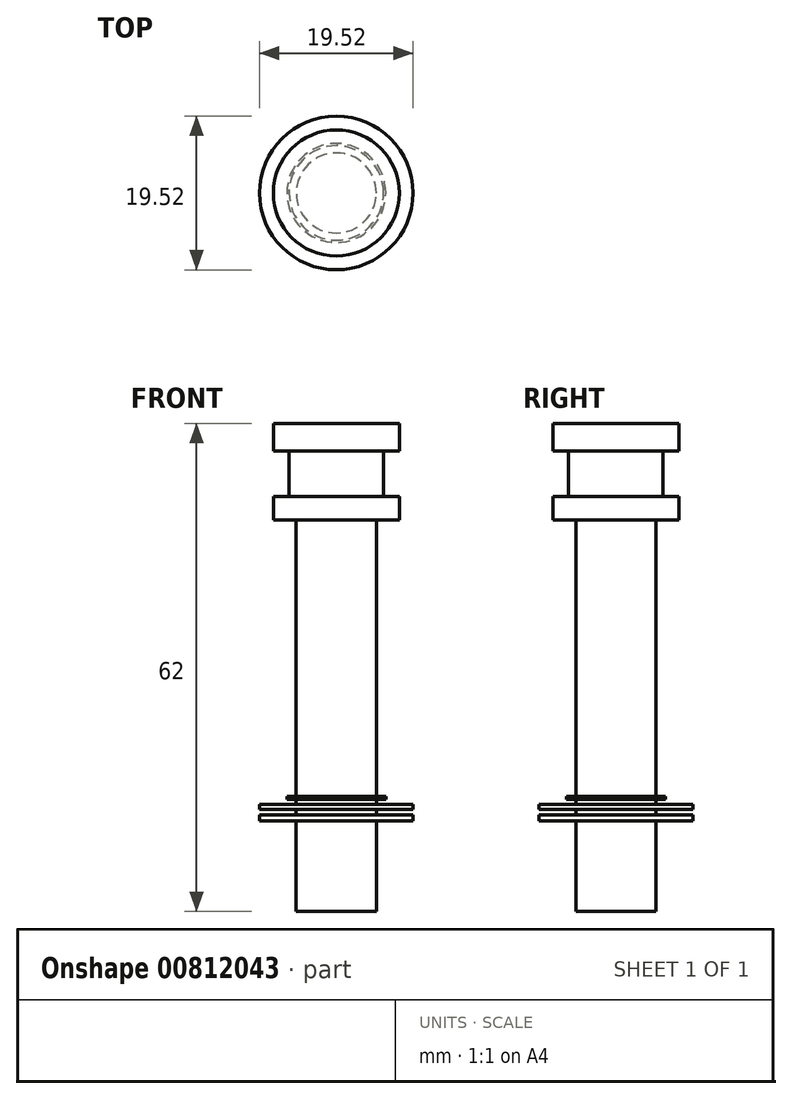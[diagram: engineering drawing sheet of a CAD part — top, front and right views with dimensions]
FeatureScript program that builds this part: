
annotation { "Feature Type Name" : "Feature", "Feature Type Description" : "" }
export const myFeature = defineFeature(function(context is Context, id is Id, definition is map)
    precondition{}
    {
        {
            var Q0;
            Q0=qCreatedBy(makeId("Front.planeOp"),FACE);
            var sketch = newSketch(context, id + "F0", { "sketchPlane" : qUnion([Q0])});
            skLineSegment(sketch, "E0", {"start": v(0, 0) * mm, "end": v(-8, 0) * mm});
            skLineSegment(sketch, "E1", {"start": v(-8, 0) * mm, "end": v(-8, -3.5) * mm});
            skLineSegment(sketch, "E2", {"start": v(-8, -3.5) * mm, "end": v(-6, -3.5) * mm});
            skLineSegment(sketch, "E3", {"start": v(-6, -3.5) * mm, "end": v(-6, -9.3) * mm});
            skLineSegment(sketch, "E4", {"start": v(-6, -9.3) * mm, "end": v(-8, -9.3) * mm});
            skLineSegment(sketch, "E5", {"start": v(-8, -9.3) * mm, "end": v(-8, -12.3) * mm});
            skLineSegment(sketch, "E6", {"start": v(-8, -12.3) * mm, "end": v(-5.09, -12.3) * mm});
            skLineSegment(sketch, "E7", {"start": v(-5.09, -12.3) * mm, "end": v(-5.09, -47.38) * mm});
            skLineSegment(sketch, "E8", {"start": v(-5.09, -47.38) * mm, "end": v(-6.29, -47.38) * mm});
            skLineSegment(sketch, "E9", {"start": v(-6.29, -47.38) * mm, "end": v(-6.29, -47.8) * mm});
            skLineSegment(sketch, "E10", {"start": v(-6.29, -47.8) * mm, "end": v(-5.09, -47.8) * mm});
            skLineSegment(sketch, "E11", {"start": v(-5.09, -47.8) * mm, "end": v(-5.09, -48.43) * mm});
            skLineSegment(sketch, "E12", {"start": v(-5.09, -48.43) * mm, "end": v(-9.76, -48.43) * mm});
            skLineSegment(sketch, "E13", {"start": v(-9.76, -48.43) * mm, "end": v(-9.76, -49.06) * mm});
            skLineSegment(sketch, "E14", {"start": v(-9.76, -49.06) * mm, "end": v(-5.09, -49.06) * mm});
            skLineSegment(sketch, "E15", {"start": v(-5.09, -49.06) * mm, "end": v(-5.09, -49.73) * mm});
            skLineSegment(sketch, "E16", {"start": v(-5.09, -49.73) * mm, "end": v(-9.76, -49.73) * mm});
            skLineSegment(sketch, "E17", {"start": v(-9.76, -49.73) * mm, "end": v(-9.76, -50.48) * mm});
            skLineSegment(sketch, "E18", {"start": v(-9.76, -50.48) * mm, "end": v(-5.09, -50.48) * mm});
            skLineSegment(sketch, "E19", {"start": v(-5.09, -50.48) * mm, "end": v(-5.09, -62) * mm});
            skLineSegment(sketch, "E20", {"start": v(-5.09, -62) * mm, "end": v(0, -62) * mm});
            skLineSegment(sketch, "E21", {"start": v(0, -62) * mm, "end": v(0, 0) * mm});
            skSolve(sketch);
        }
        {
            var Q0;
            Q0=makeQuery(id+"F0.imprint","IMPRINT",FACE,{"disambiguationData":[TD([[makeQuery(id+"F0.imprint","IMPRINT",EDGE,{"derivedFrom":sQuery(id+"F0.wireOp",EDGE,"E0")}),1.0]])]});
            var Q1;
            Q1=sQuery(id+"F0.wireOp",EDGE,"E21");
            revolve(context, id + "F1", {"surfaceOperationType" : NewSurfaceOperationType.NEW, "entities" : qUnion([Q0]), "axis" : qUnion([Q1]), "revolveType" : RevolveType.FULL});
        }
    });
